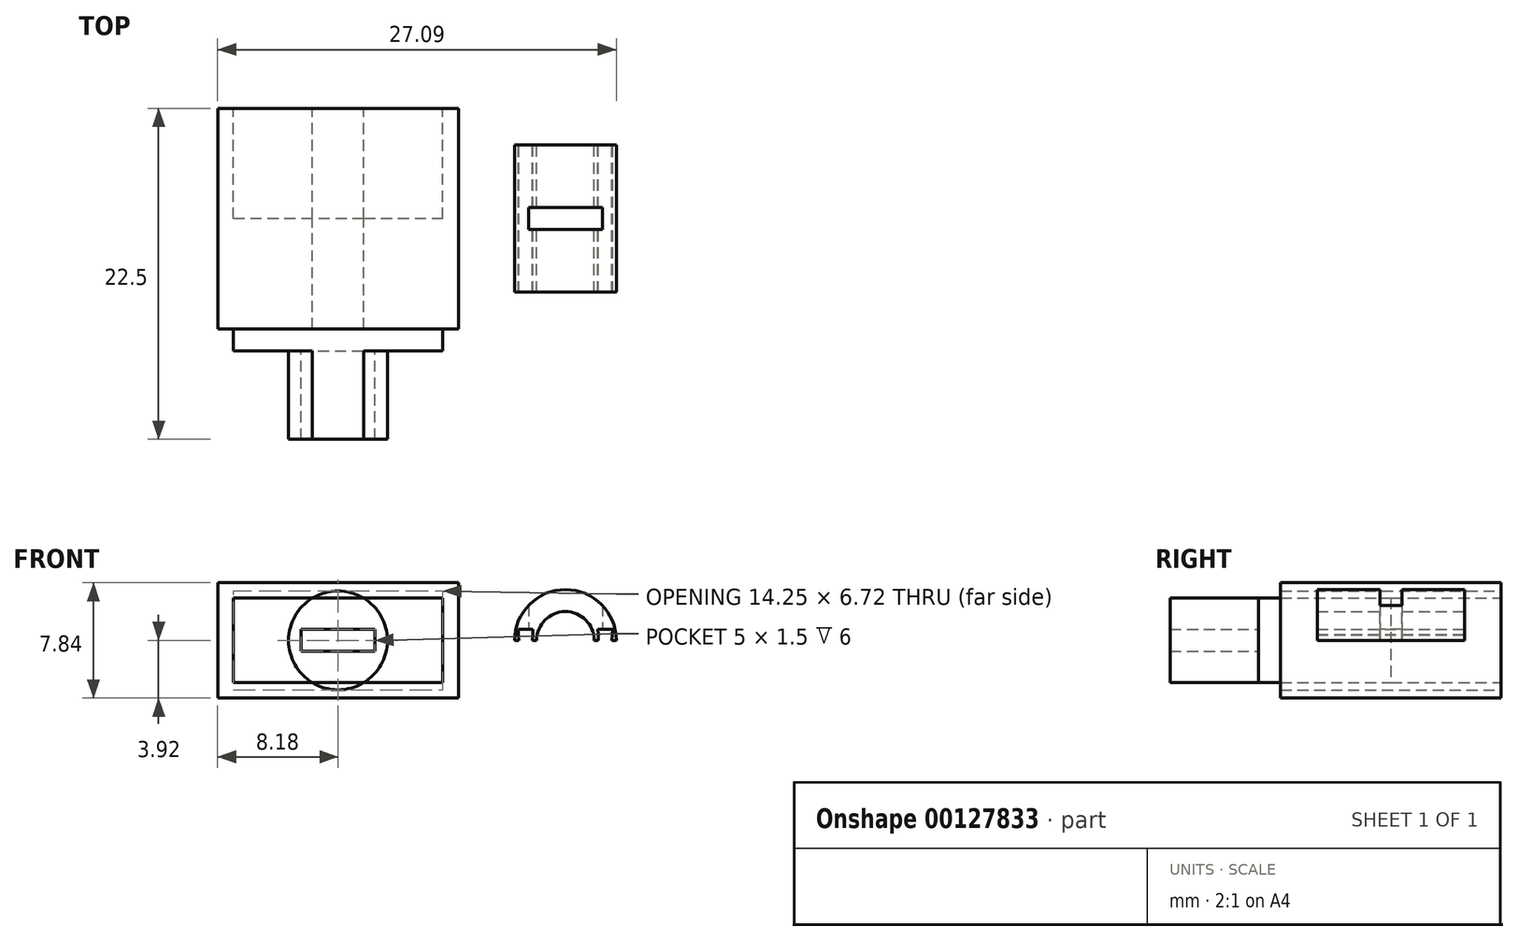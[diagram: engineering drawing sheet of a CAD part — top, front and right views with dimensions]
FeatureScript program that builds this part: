
annotation { "Feature Type Name" : "Feature", "Feature Type Description" : "" }
export const myFeature = defineFeature(function(context is Context, id is Id, definition is map)
    precondition{}
    {
        {
            var Q0;
            Q0=qCreatedBy(makeId("Front.planeOp"),FACE);
            var sketch = newSketch(context, id + "F0", { "sketchPlane" : qUnion([Q0])});
            skLineSegment(sketch, "E0.bottom", {"start": v(7.13, 2.87) * mm, "end": v(-7.12, 2.88) * mm});
            skLineSegment(sketch, "E0.top", {"start": v(7.12, -2.88) * mm, "end": v(-7.13, -2.87) * mm});
            skLineSegment(sketch, "E0.left", {"start": v(7.13, 2.87) * mm, "end": v(7.12, -2.88) * mm});
            skLineSegment(sketch, "E0.right", {"start": v(-7.12, 2.88) * mm, "end": v(-7.13, -2.87) * mm});
            skPoint(sketch, "E0.middle", {"position": v(0, 0) * mm});
            skLineSegment(sketch, "E1.0", {"start": v(-8.18, 3.93) * mm, "end": v(-8.18, -3.92) * mm});
            skLineSegment(sketch, "E1.1", {"start": v(8.18, 3.92) * mm, "end": v(-8.18, 3.93) * mm});
            skLineSegment(sketch, "E1.2", {"start": v(8.18, 3.92) * mm, "end": v(8.18, -3.93) * mm});
            skLineSegment(sketch, "E1.3", {"start": v(8.18, -3.93) * mm, "end": v(-8.18, -3.92) * mm});
            skCircle(sketch, "E2", {"center": v(0, 0) * mm, "radius": 3.36 * mm});
            skArc(sketch, "E3", {"start": v(17.4, 0) * mm, "mid": v(15.45, 1.96) * mm, "end": v(13.5, 0) * mm});
            skArc(sketch, "E4.0", {"start": v(18.9, 0) * mm, "mid": v(15.45, 3.46) * mm, "end": v(12, 0) * mm});
            skLineSegment(sketch, "E5.bottom", {"start": v(2.5, 0.75) * mm, "end": v(-2.5, 0.75) * mm});
            skLineSegment(sketch, "E5.top", {"start": v(2.5, -0.75) * mm, "end": v(-2.5, -0.75) * mm});
            skLineSegment(sketch, "E5.left", {"start": v(2.5, 0.75) * mm, "end": v(2.5, -0.75) * mm});
            skLineSegment(sketch, "E5.right", {"start": v(-2.5, 0.75) * mm, "end": v(-2.5, -0.75) * mm});
            skLineSegment(sketch, "E6", {"start": v(12, 0) * mm, "end": v(12.29, 0) * mm});
            skLineSegment(sketch, "E7.trimOffspring", {"start": v(17.4, 0) * mm, "end": v(17.7, 0) * mm});
            skLineSegment(sketch, "E8.top", {"start": v(18.66, 0.75) * mm, "end": v(17.66, 0.75) * mm});
            skPoint(sketch, "E8.middle", {"position": v(18.16, 0) * mm});
            skLineSegment(sketch, "E9", {"start": v(18.66, 0.75) * mm, "end": v(18.62, 0) * mm});
            skLineSegment(sketch, "E10", {"start": v(17.66, 0.75) * mm, "end": v(17.7, 0) * mm});
            skArc(sketch, "E11", {"start": v(17.67, 0.41) * mm, "mid": v(17.68, 0.4) * mm, "end": v(17.68, 0.38) * mm});
            skArc(sketch, "E12.MirrorCS", {"start": v(18.64, 0.41) * mm, "mid": v(18.64, 0.4) * mm, "end": v(18.64, 0.38) * mm});
            skArc(sketch, "E13.MirrorCS", {"start": v(12.27, 0.41) * mm, "mid": v(12.27, 0.4) * mm, "end": v(12.27, 0.38) * mm});
            skLineSegment(sketch, "E14.MirrorCS", {"start": v(12.25, 0.75) * mm, "end": v(12.29, 0) * mm});
            skArc(sketch, "E15.MirrorCS", {"start": v(13.23, 0.41) * mm, "mid": v(13.23, 0.4) * mm, "end": v(13.23, 0.38) * mm});
            skPoint(sketch, "E16.MirrorP", {"position": v(12.75, 0) * mm});
            skLineSegment(sketch, "E17.MirrorCS", {"start": v(13.25, 0.75) * mm, "end": v(13.21, 0) * mm});
            skLineSegment(sketch, "E18.MirrorCS", {"start": v(12.25, 0.75) * mm, "end": v(13.25, 0.75) * mm});
            skLineSegment(sketch, "E19", {"start": v(19.15, -0.18) * mm, "end": v(19.44, -0.18) * mm});
            skArc(sketch, "E20", {"start": v(24.21, -1.29) * mm, "mid": v(24.47, -0.76) * mm, "end": v(24.56, -0.18) * mm});
            skArc(sketch, "E21.0", {"start": v(24.87, -2.79) * mm, "mid": v(25.75, -1.61) * mm, "end": v(26.06, -0.18) * mm});
            skArc(sketch, "E22", {"start": v(20.65, -0.18) * mm, "mid": v(22.6, -2.13) * mm, "end": v(24.56, -0.18) * mm});
            skArc(sketch, "E23", {"start": v(19.15, -0.18) * mm, "mid": v(22.6, -3.63) * mm, "end": v(26.06, -0.18) * mm});
            skLineSegment(sketch, "E24.trimOffspring", {"start": v(24.56, -0.18) * mm, "end": v(24.85, -0.18) * mm});
            skArc(sketch, "E25.trimOffspring", {"start": v(20.65, -0.18) * mm, "mid": v(20.69, -0.55) * mm, "end": v(20.79, -0.9) * mm});
            skArc(sketch, "E26.trimOffspring", {"start": v(19.15, -0.18) * mm, "mid": v(19.32, -1.25) * mm, "end": v(19.81, -2.22) * mm});
            skLineSegment(sketch, "E27.top", {"start": v(25.56, 0.57) * mm, "end": v(25.06, 0.57) * mm});
            skPoint(sketch, "E27.middle", {"position": v(25.31, -0.18) * mm});
            skLineSegment(sketch, "E28", {"start": v(25.8, 0.23) * mm, "end": v(25.77, -0.18) * mm});
            skLineSegment(sketch, "E29", {"start": v(24.83, 0.23) * mm, "end": v(24.85, -0.18) * mm});
            skArc(sketch, "E30", {"start": v(25.06, 0.57) * mm, "mid": v(24.88, 0.42) * mm, "end": v(24.83, 0.2) * mm});
            skArc(sketch, "E31.MirrorCS", {"start": v(25.56, 0.57) * mm, "mid": v(25.74, 0.42) * mm, "end": v(25.8, 0.2) * mm});
            skArc(sketch, "E32.MirrorCS", {"start": v(20.34, -2.79) * mm, "mid": v(19.46, -1.61) * mm, "end": v(19.15, -0.18) * mm});
            skArc(sketch, "E33.MirrorCS", {"start": v(19.66, 0.57) * mm, "mid": v(19.47, 0.42) * mm, "end": v(19.42, 0.2) * mm});
            skLineSegment(sketch, "E34.MirrorCS", {"start": v(19.42, 0.23) * mm, "end": v(19.44, -0.18) * mm});
            skArc(sketch, "E35.MirrorCS", {"start": v(20.15, 0.57) * mm, "mid": v(20.33, 0.42) * mm, "end": v(20.38, 0.2) * mm});
            skPoint(sketch, "E36.MirrorP", {"position": v(19.9, -0.18) * mm});
            skLineSegment(sketch, "E37.MirrorCS", {"start": v(20.38, 0.23) * mm, "end": v(20.36, -0.18) * mm});
            skLineSegment(sketch, "E38.MirrorCS", {"start": v(19.66, 0.57) * mm, "end": v(20.15, 0.57) * mm});
            skLineSegment(sketch, "E39.trimOffspring", {"start": v(20.36, -0.18) * mm, "end": v(20.65, -0.18) * mm});
            skPoint(sketch, "E40.orphan", {"position": v(25.81, 0.57) * mm});
            skPoint(sketch, "E41.orphan", {"position": v(24.81, 0.57) * mm});
            skPoint(sketch, "E27.bottom.end.orphan", {"position": v(24.81, -0.93) * mm});
            skPoint(sketch, "E27.left.start.orphan", {"position": v(25.81, -0.93) * mm});
            skLineSegment(sketch, "E42.trimOffspring", {"start": v(25.77, -0.18) * mm, "end": v(26.06, -0.18) * mm});
            skPoint(sketch, "E43.orphan", {"position": v(18.4, 0.75) * mm});
            skPoint(sketch, "E44.orphan", {"position": v(17.91, 0.75) * mm});
            skPoint(sketch, "E8.bottom.end.orphan", {"position": v(17.66, -0.75) * mm});
            skPoint(sketch, "E8.bottom.start.orphan", {"position": v(18.66, -0.75) * mm});
            skPoint(sketch, "E45.0.start.orphan", {"position": v(17.72, -2.6) * mm});
            skLineSegment(sketch, "E46.trimOffspring", {"start": v(18.62, 0) * mm, "end": v(18.9, 0) * mm});
            skPoint(sketch, "E47.orphan", {"position": v(12.5, 0.75) * mm});
            skPoint(sketch, "E48.orphan", {"position": v(13, 0.75) * mm});
            skPoint(sketch, "E49.orphan", {"position": v(12, 0) * mm});
            skLineSegment(sketch, "E50.trimOffspring", {"start": v(13.21, 0) * mm, "end": v(13.5, 0) * mm});
            skPoint(sketch, "E51.MirrorCS.end.orphan", {"position": v(13.25, -0.75) * mm});
            skPoint(sketch, "E51.MirrorCS.start.orphan", {"position": v(12.25, -0.75) * mm});
            skPoint(sketch, "E52.MirrorCS.start.orphan", {"position": v(13.19, -2.6) * mm});
            skPoint(sketch, "E53.end.orphan", {"position": v(15.45, 1.96) * mm});
            skSolve(sketch);
        }
        {
            var Q0;
            {var subQ1=sQuery(id+"F0.wireOp",EDGE,"E0.left");Q0=makeQuery(id+"F0.imprint","IMPRINT",FACE,{"disambiguationData":[TD([[makeQuery(id+"F0.imprint","IMPRINT",EDGE,{"derivedFrom":subQ1}),1.0]])]});}
            var Q1;
            {var subQ0=sQuery(id+"F0.wireOp",EDGE,"E2");var subQ1=sQuery(id+"F0.wireOp",EDGE,"E0.top");var subQ2=makeQuery(id+"F0.imprint","INTERSECT",VERTEX,{"disambiguationData":[OD(0.0)],"derivedFrom":[subQ1,subQ0]});Q1=makeQuery(id+"F0.imprint","IMPRINT",FACE,{"disambiguationData":[TD([[makeQuery(id+"F0.imprint","IMPRINT",EDGE,{"disambiguationData":[TD([[subQ2,-1.0]])],"derivedFrom":subQ1}),1.0]])]});}
            var Q2;
            {var subQ0=sQuery(id+"F0.wireOp",EDGE,"E2");var subQ1=sQuery(id+"F0.wireOp",EDGE,"E0.bottom");var subQ2=makeQuery(id+"F0.imprint","INTERSECT",VERTEX,{"disambiguationData":[OD(0.0)],"derivedFrom":[subQ1,subQ0]});Q2=makeQuery(id+"F0.imprint","IMPRINT",FACE,{"disambiguationData":[TD([[makeQuery(id+"F0.imprint","IMPRINT",EDGE,{"disambiguationData":[TD([[subQ2,-1.0]])],"derivedFrom":subQ1}),-1.0]])]});}
            extrude(context, id + "F1", {"entities" : qUnion([Q0, Q1, Q2]), "endBound" : BoundingType.SYMMETRIC, "depth" : 15 * mm});
        }
        {
            var Q0;
            {var subQ0=sQuery(id+"F0.wireOp",EDGE,"E0.left");Q0=makeQuery(id+"F0.imprint","IMPRINT",FACE,{"disambiguationData":[TD([[makeQuery(id+"F0.imprint","IMPRINT",EDGE,{"derivedFrom":subQ0}),-1.0]])]});}
            var Q1;
            Q1=makeQuery(id+"F0.imprint","IMPRINT",FACE,{"disambiguationData":[TD([[makeQuery(id+"F0.imprint","IMPRINT",EDGE,{"derivedFrom":sQuery(id+"F0.wireOp",EDGE,"E5.bottom")}),-1.0]])]});
            var Q2;
            {var subQ0=sQuery(id+"F0.wireOp",EDGE,"E0.right");Q2=makeQuery(id+"F0.imprint","IMPRINT",FACE,{"disambiguationData":[TD([[makeQuery(id+"F0.imprint","IMPRINT",EDGE,{"derivedFrom":subQ0}),1.0]])]});}
            var Q3;
            Q3=makeQuery(id+"F0.imprint","IMPRINT",FACE,{"disambiguationData":[TD([[makeQuery(id+"F0.imprint","IMPRINT",EDGE,{"derivedFrom":sQuery(id+"F0.wireOp",EDGE,"E5.bottom")}),1.0]])]});
            extrude(context, id + "F2", {"entities" : qUnion([Q0, Q1, Q2, Q3]), "operationType" : NewBodyOperationType.ADD, "depth" : 9 * mm});
        }
        {
            var Q0;
            Q0=makeQuery(id+"F0.imprint","IMPRINT",FACE,{"disambiguationData":[TD([[makeQuery(id+"F0.imprint","IMPRINT",EDGE,{"derivedFrom":sQuery(id+"F0.wireOp",EDGE,"E5.bottom")}),-1.0]])]});
            var Q1;
            Q1=sQuery(id+"F0.wireOp",EDGE,"E2");
            var Q2;
            Q2=sQuery(id+"F0.wireOp",EDGE,"E5.bottom");
            var Q3;
            Q3=sQuery(id+"F0.wireOp",EDGE,"E5.left");
            var Q4;
            Q4=sQuery(id+"F0.wireOp",EDGE,"E5.top");
            var Q5;
            Q5=sQuery(id+"F0.wireOp",EDGE,"E5.right");
            extrude(context, id + "F3", {"entities" : qUnion([Q0]), "operationType" : NewBodyOperationType.ADD, "surfaceEntities" : qUnion([Q1, Q2, Q3, Q4, Q5]), "depth" : 15 * mm});
        }
        {
            var Q0;
            Q0=makeQuery(id+"F0.imprint","IMPRINT",FACE,{"disambiguationData":[TD([[makeQuery(id+"F0.imprint","IMPRINT",EDGE,{"derivedFrom":sQuery(id+"F0.wireOp",EDGE,"E3")}),-1.0]])]});
            var Q1;
            Q1=makeQuery(id+"F0.imprint","IMPRINT",FACE,{"disambiguationData":[TD([[makeQuery(id+"F0.imprint","IMPRINT",EDGE,{"derivedFrom":sQuery(id+"F0.wireOp",EDGE,"E6")}),-1.0]])]});
            var Q2;
            {var subQ4=sQuery(id+"F0.wireOp",EDGE,"E19");Q2=makeQuery(id+"F0.imprint","IMPRINT",FACE,{"disambiguationData":[TD([[makeQuery(id+"F0.imprint","IMPRINT",EDGE,{"derivedFrom":subQ4}),-1.0]])]});}
            extrude(context, id + "F4", {"entities" : qUnion([Q0, Q1, Q2]), "endBound" : BoundingType.SYMMETRIC, "depth" : 10 * mm});
        }
        {
            var Q0;
            Q0=qCreatedBy(makeId("Top.planeOp"),FACE);
            var sketch = newSketch(context, id + "F5", { "sketchPlane" : qUnion([Q0])});
            skLineSegment(sketch, "E54.bottom", {"start": v(17.95, -0.75) * mm, "end": v(12.95, -0.75) * mm});
            skLineSegment(sketch, "E54.top", {"start": v(17.95, 0.75) * mm, "end": v(12.95, 0.75) * mm});
            skLineSegment(sketch, "E54.left", {"start": v(17.95, -0.75) * mm, "end": v(17.95, 0.75) * mm});
            skLineSegment(sketch, "E54.right", {"start": v(12.95, -0.75) * mm, "end": v(12.95, 0.75) * mm});
            skPoint(sketch, "E54.middle", {"position": v(15.45, 0) * mm});
            skSolve(sketch);
        }
        {
            var Q0;
            Q0=makeQuery(id+"F5.imprint","IMPRINT",FACE,{"disambiguationData":[TD([[makeQuery(id+"F5.imprint","IMPRINT",EDGE,{"derivedFrom":sQuery(id+"F5.wireOp",EDGE,"E54.bottom")}),-1.0]])]});
            extrude(context, id + "F6", {"entities" : qUnion([Q0]), "operationType" : NewBodyOperationType.REMOVE, "depth" : 9.75 * mm});
        }
    });
